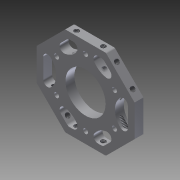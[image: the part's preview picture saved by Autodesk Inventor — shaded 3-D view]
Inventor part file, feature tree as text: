
AUTODESK INVENTOR PART (.ipt)
format: ipt  version: 2012 (Build 160160000, 160)  size: 346,624 bytes
history: native  units: in
note: dims shown in document units (in); Inventor stores cm internally (conversion verified against a paired STEP export)
features: thread x12, sketch x7, extrude x7, fillet x2
ambient origin geometry x8: Origin, YZ Plane, XZ Plane, XY Plane, X Axis, Y Axis, Z Axis, Center Point
bodies: Solid1 (feature_tree)
feature tree (28):
  sketch  "Sketch1"  dims[d0=2.75in d1=2.5in d2=1.375in d3=1.25in]
  extrude  "Extrusion1"  Depth=2.5in
  fillet  "Fillet1"  Radius=1.375in
  fillet  "Fillet2"  Radius=1.25in
  extrude  "Extrusion3"  TaperAngle=45.0deg  [1 undecoded]
  sketch  "Sketch3"  dims[d8=45.0deg d10=0.136in]
  extrude  "Extrusion4"  Depth=0.136in
  extrude  "Extrusion5"  Depth=1.125in
  extrude  "Extrusion6"  Depth=0.1875in
  extrude  "Extrusion7"  Depth=0.1875in
  extrude  "Extrusion8"  Depth=0.1875in
  thread  "Thread1"  [1 undecoded]
  thread  "Thread2"  [1 undecoded]
  thread  "Thread3"  [1 undecoded]
  thread  "Thread4"  [1 undecoded]
  thread  "Thread5"  [1 undecoded]
  thread  "Thread6"  [1 undecoded]
  thread  "Thread7"  [1 undecoded]
  thread  "Thread8"  [1 undecoded]
  thread  "Thread9"  [1 undecoded]
  thread  "Thread10"  [1 undecoded]
  thread  "Thread11"  [1 undecoded]
  thread  "Thread12"  [1 undecoded]
  sketch  "Sketch2"  dims[d6=45.0deg d7=45.0deg]
  sketch  "Sketch4"  dims[d11=0.938in d18=1.125in]
  sketch  "Sketch6"  dims[d20=2.3622in d22=360.0deg d24=0.1875in]
  sketch  "Sketch7"  dims[d25=0.1875in d26=0.1875in]
  sketch  "Sketch8"  dims[d27=0.1875in d28=0.1875in d29=0.1875in d30=0.1875in d32=0.1875in d33=0.5in d34=0.25in d35=0.0in d38=0.125in d39=0.125in d40=0.0625in d41=0.75in d42=0.1687in d43=0.1687in d44=0.136in d45=0.125in d46=0.25in d47=0.0in d48=0.125in d49=0.136in d50=0.25in d51=0.625in d52=0.125in d53=0.25in d54=0.625in d55=0.136in d56=0.625in d57=0.0in d58=0.625in d59=0.0in d61=0.75in d62=0.136in d63=0.1687in d64=0.1687in d65=0.125in d66=0.25in d67=0.0in d68=0.25in d69=0.625in d70=0.136in d71=0.125in d72=0.625in d73=0.0in d74=0.25in d75=0.125in d76=0.625in d77=0.136in d78=0.625in d79=0.0in d80=1.0in d81=0.0in d82=1.0in d83=0.0in d84=1.0in d85=0.0in d86=1.0in d87=0.0in d88=1.0in d89=0.0in d90=1.0in d91=0.0in d92=1.0in d93=0.0in d94=1.0in d95=0.0in d96=1.0in d97=0.0in d98=1.0in d99=0.0in d100=1.0in d101=0.0in d102=1.0in d103=0.0in d104=3.125in]
note: 13 required parameter values undecoded (feature->parameter linkage not recoverable at this tier; creation-order binding heuristic only, values carry confidence <= 0.55)
